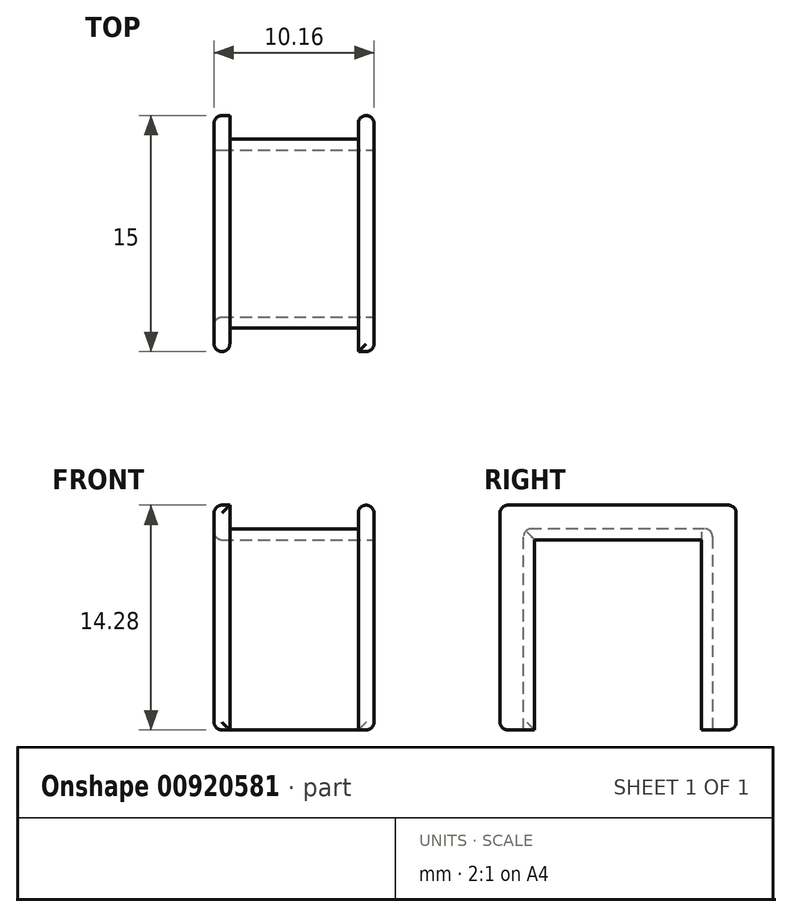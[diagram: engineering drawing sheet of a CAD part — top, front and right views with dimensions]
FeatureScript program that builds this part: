
annotation { "Feature Type Name" : "Feature", "Feature Type Description" : "" }
export const myFeature = defineFeature(function(context is Context, id is Id, definition is map)
    precondition{}
    {
        {
            var Q0;
            Q0=qCreatedBy(makeId("Top.planeOp"),FACE);
            var sketch = newSketch(context, id + "F0", { "sketchPlane" : qUnion([Q0])});
            skLineSegment(sketch, "E0.bottom", {"start": v(5.08, 7.5) * mm, "end": v(-5.08, 7.5) * mm});
            skLineSegment(sketch, "E0.top", {"start": v(5.08, -7.5) * mm, "end": v(-5.08, -7.5) * mm});
            skLineSegment(sketch, "E0.left", {"start": v(5.08, 7.5) * mm, "end": v(5.08, -7.5) * mm});
            skLineSegment(sketch, "E0.right", {"start": v(-5.08, 7.5) * mm, "end": v(-5.08, -7.5) * mm});
            skSolve(sketch);
        }
        {
            var Q0;
            Q0 = qSketchRegion(id + "F0", true);
            extrude(context, id + "F1", {"entities" : qUnion([Q0]), "depth" : 14.28 * mm, "offsetDistance" : 25 * mm});
        }
        {
            var Q0;
            Q0=makeQuery(id+"F1.opExtrude","SWEPT_FACE",FACE,{"disambiguationData":[OSD([sQuery(id+"F0.wireOp",EDGE,"E0.top")])]});
            var sketch = newSketch(context, id + "F2", { "sketchPlane" : qUnion([Q0])});
            skLineSegment(sketch, "E1.bottom", {"start": v(4.08, 0) * mm, "end": v(-4.08, 0) * mm});
            skLineSegment(sketch, "E1.top", {"start": v(4.08, 28.56) * mm, "end": v(-4.08, 28.56) * mm});
            skLineSegment(sketch, "E1.left", {"start": v(4.08, 0) * mm, "end": v(4.08, 28.56) * mm});
            skLineSegment(sketch, "E1.right", {"start": v(-4.08, 0) * mm, "end": v(-4.08, 28.56) * mm});
            skPoint(sketch, "E1.middle", {"position": v(0, 14.28) * mm});
            skSolve(sketch);
        }
        {
            var Q0;
            Q0=makeQuery(id+"F1.opExtrude","CAP_FACE",FACE,{"disambiguationData":[OSD([sQuery(id+"F0.wireOp",EDGE,"E0.bottom"),sQuery(id+"F0.wireOp",EDGE,"E0.top"),sQuery(id+"F0.wireOp",EDGE,"E0.left"),sQuery(id+"F0.wireOp",EDGE,"E0.right")])],"isStart":false});
            var sketch = newSketch(context, id + "F3", { "sketchPlane" : qUnion([Q0])});
            skLineSegment(sketch, "E2.bottom", {"start": v(4.08, 10.99) * mm, "end": v(-4.08, 10.99) * mm});
            skLineSegment(sketch, "E2.top", {"start": v(4.08, -10.99) * mm, "end": v(-4.08, -10.99) * mm});
            skLineSegment(sketch, "E2.left", {"start": v(4.08, 10.99) * mm, "end": v(4.08, -10.99) * mm});
            skLineSegment(sketch, "E2.right", {"start": v(-4.08, 10.99) * mm, "end": v(-4.08, -10.99) * mm});
            skPoint(sketch, "E2.middle", {"position": v(0, 0) * mm});
            skSolve(sketch);
        }
        {
            var Q0;
            Q0=makeQuery(id+"F1.opExtrude","SWEPT_FACE",FACE,{"disambiguationData":[OSD([sQuery(id+"F0.wireOp",EDGE,"E0.bottom")])]});
            var sketch = newSketch(context, id + "F4", { "sketchPlane" : qUnion([Q0])});
            skLineSegment(sketch, "E3.bottom", {"start": v(4.08, 21.55) * mm, "end": v(-4.08, 21.55) * mm});
            skLineSegment(sketch, "E3.top", {"start": v(4.08, -21.55) * mm, "end": v(-4.08, -21.55) * mm});
            skLineSegment(sketch, "E3.left", {"start": v(4.08, 21.55) * mm, "end": v(4.08, -21.55) * mm});
            skLineSegment(sketch, "E3.right", {"start": v(-4.08, 21.55) * mm, "end": v(-4.08, -21.55) * mm});
            skPoint(sketch, "E3.middle", {"position": v(0, 0) * mm});
            skSolve(sketch);
        }
        {
            var Q0;
            {var subQ0=sQuery(id+"F2.wireOp",EDGE,"E1.bottom");Q0=makeQuery(id+"F2.imprint","IMPRINT",FACE,{"disambiguationData":[TD([[makeQuery(id+"F2.imprint","IMPRINT",EDGE,{"derivedFrom":subQ0}),-1.0]])]});}
            extrude(context, id + "F5", {"entities" : qUnion([Q0]), "operationType" : NewBodyOperationType.REMOVE, "oppositeDirection" : true, "depth" : 1.5 * mm, "offsetDistance" : 25 * mm});
        }
        {
            var Q0;
            {var subQ0=sQuery(id+"F3.wireOp",EDGE,"E2.left");var subQ1=makeQuery(id+"F1.opExtrude","CAP_EDGE",EDGE,{"disambiguationData":[OSD([sQuery(id+"F0.wireOp",EDGE,"E0.bottom")])],"isStart":false});var subQ2=makeQuery(id+"F3.imprint","INTERSECT",VERTEX,{"derivedFrom":[subQ1,subQ0]});Q0=makeQuery(id+"F3.imprint","IMPRINT",FACE,{"disambiguationData":[TD([[makeQuery(id+"F3.imprint","IMPRINT",EDGE,{"disambiguationData":[TD([[subQ2,-1.0]])],"derivedFrom":subQ0}),-1.0]])]});}
            extrude(context, id + "F6", {"entities" : qUnion([Q0]), "operationType" : NewBodyOperationType.REMOVE, "oppositeDirection" : true, "depth" : 1.5 * mm, "offsetDistance" : 25 * mm});
        }
        {
            var Q0;
            {var subQ0=sQuery(id+"F4.wireOp",EDGE,"E3.left");var subQ1=sQuery(id+"F0.wireOp",EDGE,"E0.bottom");var subQ2=makeQuery(id+"F1.opExtrude","CAP_EDGE",EDGE,{"disambiguationData":[OSD([subQ1])],"isStart":false});var subQ3=makeQuery(id+"F4.imprint","INTERSECT",VERTEX,{"derivedFrom":[subQ2,subQ0]});Q0=makeQuery(id+"F4.imprint","IMPRINT",FACE,{"disambiguationData":[TD([[makeQuery(id+"F4.imprint","IMPRINT",EDGE,{"disambiguationData":[TD([[subQ3,-1.0]])],"derivedFrom":subQ0}),-1.0]])]});}
            extrude(context, id + "F7", {"entities" : qUnion([Q0]), "operationType" : NewBodyOperationType.REMOVE, "oppositeDirection" : true, "depth" : 1.5 * mm, "offsetDistance" : 25 * mm});
        }
        {
            var Q0;
            Q0=makeQuery(id+"F1.opExtrude","SWEPT_FACE",FACE,{"disambiguationData":[OSD([sQuery(id+"F0.wireOp",EDGE,"E0.left")])]});
            var sketch = newSketch(context, id + "F8", { "sketchPlane" : qUnion([Q0])});
            skLineSegment(sketch, "E4.bottom", {"start": v(5.3, 12.08) * mm, "end": v(-5.3, 12.08) * mm});
            skLineSegment(sketch, "E4.top", {"start": v(5.3, -12.08) * mm, "end": v(-5.3, -12.08) * mm});
            skLineSegment(sketch, "E4.left", {"start": v(5.3, 12.08) * mm, "end": v(5.3, -12.08) * mm});
            skLineSegment(sketch, "E4.right", {"start": v(-5.3, 12.08) * mm, "end": v(-5.3, -12.08) * mm});
            skPoint(sketch, "E4.middle", {"position": v(0, 0) * mm});
            skSolve(sketch);
        }
        {
            var Q0;
            {var subQ0=sQuery(id+"F8.wireOp",EDGE,"E4.bottom");Q0=makeQuery(id+"F8.imprint","IMPRINT",FACE,{"disambiguationData":[TD([[makeQuery(id+"F8.imprint","IMPRINT",EDGE,{"derivedFrom":subQ0}),1.0]])]});}
            extrude(context, id + "F9", {"entities" : qUnion([Q0]), "operationType" : NewBodyOperationType.REMOVE, "oppositeDirection" : true, "depth" : 25 * mm, "offsetDistance" : 25 * mm});
        }
        {
            var Q0;
            {var subQ0=sQuery(id+"F0.wireOp",EDGE,"E0.right");var subQ1=sQuery(id+"F0.wireOp",EDGE,"E0.top");Q0=makeQuery(id+"F5.boolean.opBoolean","SPLIT",EDGE,{"disambiguationData":[TD([makeQuery(id+"F1.opExtrude","SWEPT_FACE",FACE,{"disambiguationData":[OSD([subQ0])]})])],"derivedFrom":makeQuery(id+"F1.opExtrude","CAP_EDGE",EDGE,{"disambiguationData":[OSD([subQ1])],"isStart":false})});}
            var Q1;
            {var subQ0=sQuery(id+"F0.wireOp",EDGE,"E0.left");var subQ1=sQuery(id+"F0.wireOp",EDGE,"E0.top");Q1=makeQuery(id+"F5.boolean.opBoolean","SPLIT",EDGE,{"disambiguationData":[TD([makeQuery(id+"F1.opExtrude","SWEPT_FACE",FACE,{"disambiguationData":[OSD([subQ0])]})])],"derivedFrom":makeQuery(id+"F1.opExtrude","CAP_EDGE",EDGE,{"disambiguationData":[OSD([subQ1])],"isStart":false})});}
            var Q2;
            Q2=makeQuery(id+"F5.boolean.opBoolean","COPY",EDGE,{"derivedFrom":makeQuery(id+"F5.opExtrude","CAP_EDGE",EDGE,{"disambiguationData":[OSD([sQuery(id+"F2.wireOp",EDGE,"E1.right")])],"isStart":true})});
            var Q3;
            Q3=makeQuery(id+"F1.opExtrude","SWEPT_EDGE",EDGE,{"disambiguationData":[OSD([sQuery(id+"F0.wireOp",EDGE,"E0.top"),sQuery(id+"F0.wireOp",EDGE,"E0.right")])]});
            var Q4;
            Q4=makeQuery(id+"F1.opExtrude","CAP_EDGE",EDGE,{"disambiguationData":[OSD([sQuery(id+"F0.wireOp",EDGE,"E0.right")])],"isStart":false});
            var Q5;
            Q5=makeQuery(id+"F9.boolean.opBoolean","INTERSECT",EDGE,{"derivedFrom":[makeQuery(id+"F1.opExtrude","SWEPT_FACE",FACE,{"disambiguationData":[OSD([sQuery(id+"F0.wireOp",EDGE,"E0.right")])]}),makeQuery(id+"F9.opExtrude","SWEPT_FACE",FACE,{"disambiguationData":[OSD([sQuery(id+"F8.wireOp",EDGE,"E4.bottom")])]})]});
            var Q6;
            Q6=makeQuery(id+"F9.boolean.opBoolean","INTERSECT",EDGE,{"derivedFrom":[makeQuery(id+"F1.opExtrude","SWEPT_FACE",FACE,{"disambiguationData":[OSD([sQuery(id+"F0.wireOp",EDGE,"E0.right")])]}),makeQuery(id+"F9.opExtrude","SWEPT_FACE",FACE,{"disambiguationData":[OSD([sQuery(id+"F8.wireOp",EDGE,"E4.right")])]})]});
            var Q7;
            {var subQ0=sQuery(id+"F0.wireOp",EDGE,"E0.right");var subQ1=sQuery(id+"F0.wireOp",EDGE,"E0.top");Q7=makeQuery(id+"F9.boolean.opBoolean","SPLIT",EDGE,{"disambiguationData":[TD([makeQuery(id+"F1.opExtrude","SWEPT_FACE",FACE,{"disambiguationData":[OSD([subQ1])]})])],"derivedFrom":makeQuery(id+"F1.opExtrude","CAP_EDGE",EDGE,{"disambiguationData":[OSD([subQ0])],"isStart":true})});}
            var Q8;
            {var subQ0=sQuery(id+"F0.wireOp",EDGE,"E0.right");var subQ1=sQuery(id+"F0.wireOp",EDGE,"E0.top");Q8=makeQuery(id+"F5.boolean.opBoolean","SPLIT",EDGE,{"disambiguationData":[TD([makeQuery(id+"F1.opExtrude","SWEPT_FACE",FACE,{"disambiguationData":[OSD([subQ0])]})])],"derivedFrom":makeQuery(id+"F1.opExtrude","CAP_EDGE",EDGE,{"disambiguationData":[OSD([subQ1])],"isStart":true})});}
            var Q9;
            {var subQ0=sQuery(id+"F0.wireOp",EDGE,"E0.left");var subQ1=sQuery(id+"F0.wireOp",EDGE,"E0.top");Q9=makeQuery(id+"F5.boolean.opBoolean","SPLIT",EDGE,{"disambiguationData":[TD([makeQuery(id+"F1.opExtrude","SWEPT_FACE",FACE,{"disambiguationData":[OSD([subQ0])]})])],"derivedFrom":makeQuery(id+"F1.opExtrude","CAP_EDGE",EDGE,{"disambiguationData":[OSD([subQ1])],"isStart":true})});}
            var Q10;
            Q10=makeQuery(id+"F5.boolean.opBoolean","COPY",EDGE,{"derivedFrom":makeQuery(id+"F5.opExtrude","CAP_EDGE",EDGE,{"disambiguationData":[OSD([sQuery(id+"F2.wireOp",EDGE,"E1.left")])],"isStart":true})});
            var Q11;
            Q11=makeQuery(id+"F1.opExtrude","SWEPT_EDGE",EDGE,{"disambiguationData":[OSD([sQuery(id+"F0.wireOp",EDGE,"E0.top"),sQuery(id+"F0.wireOp",EDGE,"E0.left")])]});
            var Q12;
            Q12=makeQuery(id+"F1.opExtrude","CAP_EDGE",EDGE,{"disambiguationData":[OSD([sQuery(id+"F0.wireOp",EDGE,"E0.left")])],"isStart":false});
            var Q13;
            Q13=makeQuery(id+"F6.boolean.opBoolean","MERGE",EDGE,{"derivedFrom":[makeQuery(id+"F5.boolean.opBoolean","COPY",EDGE,{"derivedFrom":makeQuery(id+"F5.opExtrude","SWEPT_EDGE",EDGE,{"disambiguationData":[OSD([sQuery(id+"F0.wireOp",EDGE,"E0.top"),sQuery(id+"F2.wireOp",EDGE,"E1.right")])]})})],"fromTools":[makeQuery(id+"F6.opExtrude","CAP_EDGE",EDGE,{"disambiguationData":[OSD([sQuery(id+"F3.wireOp",EDGE,"E2.right")])],"isStart":true})]});
            var Q14;
            Q14=makeQuery(id+"F6.boolean.opBoolean","MERGE",EDGE,{"derivedFrom":[makeQuery(id+"F5.boolean.opBoolean","COPY",EDGE,{"derivedFrom":makeQuery(id+"F5.opExtrude","SWEPT_EDGE",EDGE,{"disambiguationData":[OSD([sQuery(id+"F0.wireOp",EDGE,"E0.top"),sQuery(id+"F2.wireOp",EDGE,"E1.left")])]})})],"fromTools":[makeQuery(id+"F6.opExtrude","CAP_EDGE",EDGE,{"disambiguationData":[OSD([sQuery(id+"F3.wireOp",EDGE,"E2.left")])],"isStart":true})]});
            var Q15;
            Q15=makeQuery(id+"F1.opExtrude","SWEPT_EDGE",EDGE,{"disambiguationData":[OSD([sQuery(id+"F0.wireOp",EDGE,"E0.bottom"),sQuery(id+"F0.wireOp",EDGE,"E0.left")])]});
            var Q16;
            Q16=makeQuery(id+"F7.boolean.opBoolean","MERGE",EDGE,{"derivedFrom":[makeQuery(id+"F6.boolean.opBoolean","COPY",EDGE,{"derivedFrom":makeQuery(id+"F6.opExtrude","SWEPT_EDGE",EDGE,{"disambiguationData":[OSD([sQuery(id+"F0.wireOp",EDGE,"E0.bottom"),sQuery(id+"F3.wireOp",EDGE,"E2.left")])]})})],"fromTools":[makeQuery(id+"F7.opExtrude","CAP_EDGE",EDGE,{"disambiguationData":[OSD([sQuery(id+"F4.wireOp",EDGE,"E3.right")])],"isStart":true})]});
            var Q17;
            Q17=makeQuery(id+"F7.boolean.opBoolean","MERGE",EDGE,{"derivedFrom":[makeQuery(id+"F6.boolean.opBoolean","COPY",EDGE,{"derivedFrom":makeQuery(id+"F6.opExtrude","SWEPT_EDGE",EDGE,{"disambiguationData":[OSD([sQuery(id+"F0.wireOp",EDGE,"E0.bottom"),sQuery(id+"F3.wireOp",EDGE,"E2.right")])]})})],"fromTools":[makeQuery(id+"F7.opExtrude","CAP_EDGE",EDGE,{"disambiguationData":[OSD([sQuery(id+"F4.wireOp",EDGE,"E3.left")])],"isStart":true})]});
            var Q18;
            Q18=makeQuery(id+"F1.opExtrude","SWEPT_EDGE",EDGE,{"disambiguationData":[OSD([sQuery(id+"F0.wireOp",EDGE,"E0.bottom"),sQuery(id+"F0.wireOp",EDGE,"E0.right")])]});
            var Q19;
            {var subQ0=sQuery(id+"F0.wireOp",EDGE,"E0.right");var subQ1=sQuery(id+"F0.wireOp",EDGE,"E0.bottom");Q19=makeQuery(id+"F6.boolean.opBoolean","SPLIT",EDGE,{"disambiguationData":[TD([makeQuery(id+"F1.opExtrude","SWEPT_FACE",FACE,{"disambiguationData":[OSD([subQ0])]})])],"derivedFrom":makeQuery(id+"F1.opExtrude","CAP_EDGE",EDGE,{"disambiguationData":[OSD([subQ1])],"isStart":false})});}
            var Q20;
            {var subQ0=sQuery(id+"F0.wireOp",EDGE,"E0.bottom");var subQ1=sQuery(id+"F0.wireOp",EDGE,"E0.left");Q20=makeQuery(id+"F6.boolean.opBoolean","SPLIT",EDGE,{"disambiguationData":[TD([makeQuery(id+"F1.opExtrude","SWEPT_FACE",FACE,{"disambiguationData":[OSD([subQ1])]})])],"derivedFrom":makeQuery(id+"F1.opExtrude","CAP_EDGE",EDGE,{"disambiguationData":[OSD([subQ0])],"isStart":false})});}
            var Q21;
            {var subQ0=sQuery(id+"F0.wireOp",EDGE,"E0.bottom");var subQ1=sQuery(id+"F0.wireOp",EDGE,"E0.left");Q21=makeQuery(id+"F7.boolean.opBoolean","SPLIT",EDGE,{"disambiguationData":[TD([makeQuery(id+"F1.opExtrude","SWEPT_FACE",FACE,{"disambiguationData":[OSD([subQ1])]})])],"derivedFrom":makeQuery(id+"F1.opExtrude","CAP_EDGE",EDGE,{"disambiguationData":[OSD([subQ0])],"isStart":true})});}
            var Q22;
            {var subQ0=sQuery(id+"F0.wireOp",EDGE,"E0.right");var subQ1=sQuery(id+"F0.wireOp",EDGE,"E0.bottom");Q22=makeQuery(id+"F7.boolean.opBoolean","SPLIT",EDGE,{"disambiguationData":[TD([makeQuery(id+"F1.opExtrude","SWEPT_FACE",FACE,{"disambiguationData":[OSD([subQ0])]})])],"derivedFrom":makeQuery(id+"F1.opExtrude","CAP_EDGE",EDGE,{"disambiguationData":[OSD([subQ1])],"isStart":true})});}
            var Q23;
            {var subQ0=sQuery(id+"F0.wireOp",EDGE,"E0.bottom");var subQ1=sQuery(id+"F0.wireOp",EDGE,"E0.right");Q23=makeQuery(id+"F9.boolean.opBoolean","SPLIT",EDGE,{"disambiguationData":[TD([makeQuery(id+"F1.opExtrude","SWEPT_FACE",FACE,{"disambiguationData":[OSD([subQ0])]})])],"derivedFrom":makeQuery(id+"F1.opExtrude","CAP_EDGE",EDGE,{"disambiguationData":[OSD([subQ1])],"isStart":true})});}
            var Q24;
            {var subQ0=sQuery(id+"F4.wireOp",EDGE,"E3.left");var subQ1=sQuery(id+"F0.wireOp",EDGE,"E0.bottom");Q24=makeQuery(id+"F7.boolean.opBoolean","COPY",EDGE,{"derivedFrom":makeQuery(id+"F7.opExtrude","SWEPT_EDGE",EDGE,{"disambiguationData":[OSD([subQ1,subQ0]),TDD([makeQuery(id+"F4.imprint","INTERSECT",VERTEX,{"derivedFrom":[makeQuery(id+"F1.opExtrude","CAP_EDGE",EDGE,{"disambiguationData":[OSD([subQ1])],"isStart":true}),subQ0]})])]})});}
            var Q25;
            {var subQ0=sQuery(id+"F4.wireOp",EDGE,"E3.right");var subQ1=sQuery(id+"F0.wireOp",EDGE,"E0.bottom");Q25=makeQuery(id+"F7.boolean.opBoolean","COPY",EDGE,{"derivedFrom":makeQuery(id+"F7.opExtrude","SWEPT_EDGE",EDGE,{"disambiguationData":[OSD([subQ1,subQ0]),TDD([makeQuery(id+"F4.imprint","INTERSECT",VERTEX,{"derivedFrom":[makeQuery(id+"F1.opExtrude","CAP_EDGE",EDGE,{"disambiguationData":[OSD([subQ1])],"isStart":true}),subQ0]})])]})});}
            var Q26;
            {var subQ0=sQuery(id+"F0.wireOp",EDGE,"E0.bottom");var subQ1=sQuery(id+"F0.wireOp",EDGE,"E0.left");Q26=makeQuery(id+"F9.boolean.opBoolean","SPLIT",EDGE,{"disambiguationData":[TD([makeQuery(id+"F1.opExtrude","SWEPT_FACE",FACE,{"disambiguationData":[OSD([subQ0])]})])],"derivedFrom":makeQuery(id+"F1.opExtrude","CAP_EDGE",EDGE,{"disambiguationData":[OSD([subQ1])],"isStart":true})});}
            var Q27;
            {var subQ0=sQuery(id+"F0.wireOp",EDGE,"E0.left");var subQ1=sQuery(id+"F0.wireOp",EDGE,"E0.top");Q27=makeQuery(id+"F9.boolean.opBoolean","SPLIT",EDGE,{"disambiguationData":[TD([makeQuery(id+"F1.opExtrude","SWEPT_FACE",FACE,{"disambiguationData":[OSD([subQ1])]})])],"derivedFrom":makeQuery(id+"F1.opExtrude","CAP_EDGE",EDGE,{"disambiguationData":[OSD([subQ0])],"isStart":true})});}
            var Q28;
            Q28=makeQuery(id+"F5.boolean.opBoolean","COPY",EDGE,{"derivedFrom":makeQuery(id+"F5.opExtrude","SWEPT_EDGE",EDGE,{"disambiguationData":[OSD([sQuery(id+"F0.wireOp",EDGE,"E0.top"),sQuery(id+"F2.wireOp",EDGE,"E1.bottom"),sQuery(id+"F2.wireOp",EDGE,"E1.right")])]})});
            var Q29;
            Q29=makeQuery(id+"F5.boolean.opBoolean","COPY",EDGE,{"derivedFrom":makeQuery(id+"F5.opExtrude","SWEPT_EDGE",EDGE,{"disambiguationData":[OSD([sQuery(id+"F0.wireOp",EDGE,"E0.top"),sQuery(id+"F2.wireOp",EDGE,"E1.bottom"),sQuery(id+"F2.wireOp",EDGE,"E1.left")])]})});
            var Q30;
            {var subQ0=sQuery(id+"F0.wireOp",EDGE,"E0.top");Q30=makeQuery(id+"F6.boolean.opBoolean","INTERSECT",EDGE,{"derivedFrom":[makeQuery(id+"F5.boolean.opBoolean","COPY",FACE,{"derivedFrom":makeQuery(id+"F5.opExtrude","CAP_FACE",FACE,{"disambiguationData":[OSD([subQ0,sQuery(id+"F2.wireOp",EDGE,"E1.bottom"),sQuery(id+"F2.wireOp",EDGE,"E1.left"),sQuery(id+"F2.wireOp",EDGE,"E1.right")])],"isStart":false})}),makeQuery(id+"F6.opExtrude","CAP_FACE",FACE,{"disambiguationData":[OSD([sQuery(id+"F0.wireOp",EDGE,"E0.bottom"),subQ0,sQuery(id+"F3.wireOp",EDGE,"E2.left"),sQuery(id+"F3.wireOp",EDGE,"E2.right")])],"isStart":false})]});}
            var Q31;
            {var subQ0=sQuery(id+"F0.wireOp",EDGE,"E0.bottom");Q31=makeQuery(id+"F7.boolean.opBoolean","INTERSECT",EDGE,{"derivedFrom":[makeQuery(id+"F6.boolean.opBoolean","COPY",FACE,{"derivedFrom":makeQuery(id+"F6.opExtrude","CAP_FACE",FACE,{"disambiguationData":[OSD([subQ0,sQuery(id+"F0.wireOp",EDGE,"E0.top"),sQuery(id+"F3.wireOp",EDGE,"E2.left"),sQuery(id+"F3.wireOp",EDGE,"E2.right")])],"isStart":false})}),makeQuery(id+"F7.opExtrude","CAP_FACE",FACE,{"disambiguationData":[OSD([subQ0,sQuery(id+"F4.wireOp",EDGE,"E3.left"),sQuery(id+"F4.wireOp",EDGE,"E3.right")])],"isStart":false})]});}
            fillet(context, id + "F10", {"entities" : qUnion([Q0, Q1, Q2, Q3, Q4, Q5, Q6, Q7, Q8, Q9, Q10, Q11, Q12, Q13, Q14, Q15, Q16, Q17, Q18, Q19, Q20, Q21, Q22, Q23, Q24, Q25, Q26, Q27, Q28, Q29, Q30, Q31]), "radius" : 0.5 * mm, "tangentPropagation" : true, "allowEdgeOverflow" : false});
        }
    });
